# Revit family: Support-Teknion-HNBFNA_Navigate_Frame-R2016
name_source: partatom
category: Furniture
revit_build: Autodesk Revit Architecture 2016 (Build: 20150220_1215(x64)
units: mm (PartAtom-declared; Revit-internal decimal feet)

## family parameters
Always vertical = Yes
Cut with Voids When Loaded = No
OmniClass Number = 23.40.20.00
OmniClass Title = General Furniture and Specialties
Room Calculation Point = No
Shared = Yes
Work Plane-Based = No

## types (3) — shared parameters
Assembly Code = E2020200
Manufacturer = Teknion
Manufacturer Fax = 416.661.4586
Part Number = HNBFNA
Product Documentation Link = https://www.teknion.com
Product Line = Navigate
Product Page URL = https://www.teknion.com
Series = Height-Adjustable Bench
Sustainability Data = https://www.teknion.com
URL = www.teknion.com
Unit Weight URL = http://www.teknion.com
Warranty = http://www.teknion.com

## per-type parameters (varying)
| type | Description | Extended Electrics Extended | Extended Electrics Restricted | Model | Not Extend Electrics Extended | Outer Leg Layer Height | Standard Electric |
| Standard Electric (27" - 43") | Navigate Frame, Standard Electric | No | No | HNBFNA7S_ | Yes | 22.736 " | Yes |
| Extended Electrics-Restricted (25" - 48.7") | Navigate Frame, Extended Electrics-Restricted | No | Yes | HNBFNA9C_ | Yes | 22.736 " | No |
| Extended Electrics-Exteneded (22.6" - 48.7") | Navigate Frame, Extended Electrics-Extended | Yes | No | HNBFNA9E_ | No | 17.953 " | No |

## geometry (parser evidence)
native form markers: Blend x2, Sweep x3
no freeform markers — native parametric forms only
